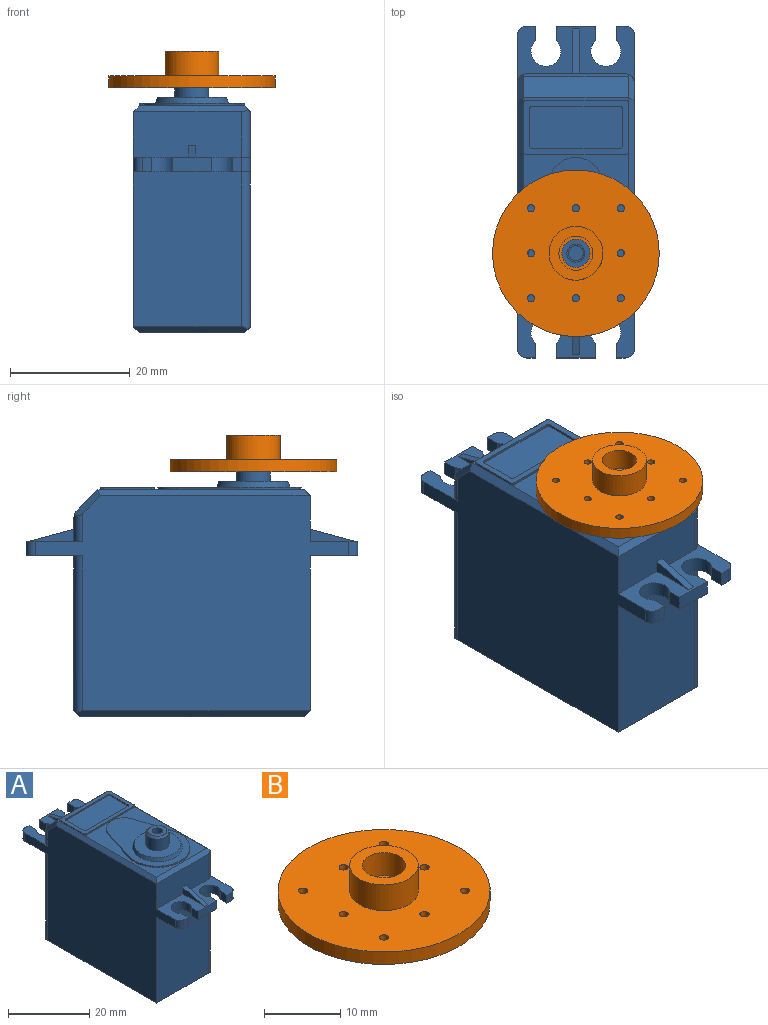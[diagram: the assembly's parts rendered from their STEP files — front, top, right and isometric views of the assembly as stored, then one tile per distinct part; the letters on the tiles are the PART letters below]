
ASSEMBLY  parts=2 mates=1
PART A: 88 faces, bbox 19.5x55.4x43.3 mm
  f0: plane 25.45x17.5mm, normal (0,0,1), area 153.9mm2, adj f42,f43,f44,f45,f56,f57,f58,f77
  f1: plane 17.5x0.91mm, normal (0,0,1), area 7.4mm2, adj f41,f56,f58,f71,f84,f85
  f2: plane 19.5x9.5mm, normal (0,0,1), area 94.3mm2, adj f3,f4,f5,f14,f15,f29,f30,f31
  f3: plane 16.5x3.98mm, normal (0,1,0), area 63.2mm2, adj f2,f36,f37,f38,f60,f61,f62
  f4: plane 2.45x1.5mm, normal (0,1,0), area 3.7mm2, adj f2,f6,f34,f40
  f5: plane 6.5x2.45mm, normal (0,1,0), area 15.9mm2, adj f2,f6,f30,f33
  f6: plane 19.5x9.5mm, normal (0,0,-1), area 103.3mm2, adj f4,f5,f7,f14,f15,f29,f30,f31
  f7: plane 25.85x16.5mm, normal (0,1,0), area 426.5mm2, adj f6,f52,f64,f65
  f8: plane 19.5x9.5mm, normal (0,0,1), area 93.8mm2, adj f9,f10,f11,f14,f15,f17,f18,f19
  f9: plane 18x7.6mm, normal (0,-1,0), area 134.4mm2, adj f8,f14,f24,f25,f26,f57,f63
  f10: plane 6.5x2.45mm, normal (0,-1,0), area 15.9mm2, adj f8,f12,f18,f23
  f11: plane 2.45x1.5mm, normal (0,-1,0), area 3.7mm2, adj f8,f12,f20,f27
  f12: plane 19.5x9.5mm, normal (0,0,-1), area 102.8mm2, adj f10,f11,f13,f14,f15,f17,f18,f19
  f13: plane 25.85x18mm, normal (0,-1,0), area 465.3mm2, adj f12,f14,f53,f66
  f14: plane 52.4x35.9mm, normal (-1,0,0), area 1391.9mm2, adj f2,f6,f8,f9,f12,f13,f27,f39
  f15: plane 52.4x35.9mm, normal (1,0,0), area 1341.7mm2, adj f2,f6,f8,f12,f28,f40,f54,f58
  f16: plane 37.4x17.5mm, normal (0,0,-1), area 654.5mm2, adj f51,f52,f53,f54
  f17: plane 2.45x1.5mm, normal (0,-1,0), area 3.7mm2, adj f8,f12,f21,f28
  f18: plane 2.45x2.41mm, normal (-1,0,0), area 5.9mm2, adj f8,f10,f12,f19
  f19: cylinder r=2.5mm len=5mm, axis (0,0,1), area 29mm2, adj f8,f12,f18,f20
  f20: plane 2.45x2.41mm, normal (1,0,0), area 5.9mm2, adj f8,f11,f12,f19
  f21: plane 2.45x2.41mm, normal (-1,0,0), area 5.9mm2, adj f8,f12,f17,f22
  f22: cylinder r=2.5mm len=5mm, axis (0,0,1), area 29mm2, adj f8,f12,f21,f23
  f23: plane 2.45x2.41mm, normal (1,0,0), area 5.9mm2, adj f8,f10,f12,f22
  f24: plane 7.5x2mm, normal (0,-0.26,0.97), area 9.3mm2, adj f8,f9,f25,f26
  f25: plane 7.5x2mm, normal (1,0,0), area 7.5mm2, adj f8,f9,f24
  f26: plane 7.5x2mm, normal (-1,0,0), area 7.5mm2, adj f8,f9,f24
  f27: cylinder r=1.5mm len=2.45mm, axis (0,0,1), area 5.8mm2, adj f8,f11,f12,f14
  f28: cylinder r=1.5mm len=2.45mm, axis (0,0,-1), area 5.8mm2, adj f8,f12,f15,f17
  f29: plane 2.45x1.5mm, normal (0,1,0), area 3.7mm2, adj f2,f6,f31,f39
  f30: plane 2.45x2.41mm, normal (-1,0,0), area 5.9mm2, adj f2,f5,f6,f32
  f31: plane 2.45x2.41mm, normal (1,0,0), area 5.9mm2, adj f2,f6,f29,f32
  f32: cylinder r=2.5mm len=5mm, axis (0,0,1), area 29mm2, adj f2,f6,f30,f31
  f33: plane 2.45x2.41mm, normal (1,0,0), area 5.9mm2, adj f2,f5,f6,f35
  f34: plane 2.45x2.41mm, normal (-1,0,0), area 5.9mm2, adj f2,f4,f6,f35
  f35: cylinder r=2.5mm len=5mm, axis (0,0,1), area 29mm2, adj f2,f6,f33,f34
  f36: plane 7.5x2mm, normal (0,0.26,0.97), area 9.3mm2, adj f2,f3,f37,f38
  f37: plane 7.5x2mm, normal (1,0,0), area 7.5mm2, adj f2,f3,f36
  f38: plane 7.5x2mm, normal (-1,0,0), area 7.5mm2, adj f2,f3,f36
  f39: cylinder r=1.5mm len=2.45mm, axis (0,0,1), area 5.8mm2, adj f2,f6,f14,f29
  f40: cylinder r=1.5mm len=2.45mm, axis (0,0,-1), area 5.8mm2, adj f2,f4,f6,f15
  f41: plane 17.5x3.56mm, normal (0,0.71,0.71), area 88.1mm2, adj f1,f55,f59,f62
  f42: cylinder r=4.5mm len=8.57mm, axis (0,0,-1), area 4.5mm2, adj f0,f43,f45,f46
  f43: plane 10.43x3.33mm, normal (-0.95,0.3,0), area 4.4mm2, adj f0,f42,f44,f46
  f44: cylinder r=8mm len=16mm, axis (0,0,-1), area 12mm2, adj f0,f43,f45,f46
  f45: plane 10.43x3.33mm, normal (0.95,0.3,0), area 4.4mm2, adj f0,f42,f44,f46
  f46: plane 24x16mm, normal (0,0,1), area 164mm2, adj f42,f43,f44,f45,f48
  f47: plane 11.5x11.5mm, normal (0,0,1), area 78.4mm2, adj f48,f49
  f48: cone r=6.15mm half-angle=21.8deg, axis (0,0,-1), area 40.3mm2, adj f46,f47
  f49: cylinder r=2.85mm len=5.7mm, axis (0,0,-1), area 62.7mm2, adj f47,f67
  f50: plane 4.7x4.7mm, normal (0,0,1), area 12.4mm2, adj f67,f68
  f51: plane 38.96x1mm, normal (-0.71,0,-0.71), area 54mm2, adj f14,f16,f52,f53,f65
  f52: plane 18.62x1mm, normal (0,0.71,-0.71), area 25.5mm2, adj f7,f16,f51,f54,f64,f65
  f53: plane 19.06x1mm, normal (0,-0.71,-0.71), area 25.8mm2, adj f13,f16,f51,f54,f66
  f54: plane 38.52x1mm, normal (0.71,0,-0.71), area 53.6mm2, adj f15,f16,f52,f53,f64,f66
  f55: plane 4.39x4.29mm, normal (-0.71,0.5,0.5), area 7.5mm2, adj f14,f41,f56,f60,f62
  f56: plane 35.4x1mm, normal (-0.71,0,0.71), area 49.1mm2, adj f0,f1,f14,f55,f57,f72
  f57: plane 19.06x1mm, normal (0,-0.71,0.71), area 25.8mm2, adj f0,f9,f56,f58,f63
  f58: plane 34.96x1mm, normal (0.71,0,0.71), area 48.7mm2, adj f0,f1,f15,f57,f59,f63,f70
  f59: plane 4.39x4.29mm, normal (0.71,0.5,0.5), area 7.5mm2, adj f15,f41,f58,f61,f62
  f60: cylinder r=1.5mm len=4.69mm, axis (0,0,1), area 10.2mm2, adj f2,f3,f14,f55,f62
  f61: cylinder r=1.5mm len=4.69mm, axis (0,0,-1), area 10.2mm2, adj f2,f3,f15,f59,f62
  f62: cylinder r=1.5mm len=17.71mm, axis (-1,0,0), area 20.4mm2, adj f3,f41,f55,f59,f60,f61
  f63: cylinder r=1.5mm len=8.04mm, axis (0,0,1), area 18.3mm2, adj f8,f9,f15,f57,f58
  f64: cylinder r=1.5mm len=26.29mm, axis (0,0,-1), area 61.3mm2, adj f6,f7,f15,f52,f54
  f65: cylinder r=1.5mm len=26.29mm, axis (0,0,1), area 61.3mm2, adj f6,f7,f14,f51,f52
  f66: cylinder r=1.5mm len=26.29mm, axis (0,0,1), area 61.3mm2, adj f12,f13,f15,f53,f54
  f67: cone r=2.35mm half-angle=45deg, axis (0,0,-1), area 11.6mm2, adj f49,f50
  f68: cylinder r=1.25mm len=8mm, axis (0,0,1), area 62.8mm2, adj f50,f69
  f69: plane 2.5x2.5mm, normal (0,0,1), area 4.9mm2, adj f68
  f70: plane 8.04x0.4mm, normal (1,0,0), area 3.2mm2, adj f58,f78,f84,f87
  f71: plane 16.5x0.4mm, normal (0,1,0), area 6.6mm2, adj f1,f78,f84,f85
  f72: plane 8.04x0.4mm, normal (-1,0,0), area 3.2mm2, adj f56,f78,f85,f86
  f73: plane 14.5x0.4mm, normal (0,-1,0), area 5.8mm2, adj f78,f79,f80,f83
  f74: plane 6.04x0.4mm, normal (-1,0,0), area 2.4mm2, adj f78,f79,f80,f81
  f75: plane 14.5x0.4mm, normal (0,1,0), area 5.8mm2, adj f78,f79,f81,f82
  f76: plane 6.04x0.4mm, normal (1,0,0), area 2.4mm2, adj f78,f79,f82,f83
  f77: plane 16.5x0.4mm, normal (0,-1,0), area 6.6mm2, adj f0,f78,f86,f87
  f78: plane 17.5x9.04mm, normal (0,0,1), area 49.1mm2, adj f70,f71,f72,f73,f74,f75,f76,f77
  f79: plane 15.5x7.04mm, normal (0,0,1), area 108.8mm2, adj f73,f74,f75,f76,f80,f81,f82,f83
  f80: cylinder r=0.5mm len=0.5mm, axis (0,0,-1), area 0.3mm2, adj f73,f74,f78,f79
  f81: cylinder r=0.5mm len=0.5mm, axis (0,0,1), area 0.3mm2, adj f74,f75,f78,f79
  f82: cylinder r=0.5mm len=0.5mm, axis (0,0,-1), area 0.3mm2, adj f75,f76,f78,f79
  f83: cylinder r=0.5mm len=0.5mm, axis (0,0,1), area 0.3mm2, adj f73,f76,f78,f79
  f84: cylinder r=0.5mm len=0.5mm, axis (0,0,-1), area 0.3mm2, adj f1,f70,f71,f78
  f85: cylinder r=0.5mm len=0.5mm, axis (0,0,-1), area 0.3mm2, adj f1,f71,f72,f78
  f86: cylinder r=0.5mm len=0.5mm, axis (0,0,1), area 0.3mm2, adj f0,f72,f77,f78
  f87: cylinder r=0.5mm len=0.5mm, axis (0,0,1), area 0.3mm2, adj f0,f70,f77,f78
PART B: 18 faces, bbox 27.8x27.8x6.1 mm
  f0: cylinder r=1.5mm len=3mm, axis (0,0,-1), area 8.5mm2, adj f7,f8
  f1: cylinder r=13.9mm len=27.8mm, axis (0,0,-1), area 174.7mm2, adj f2,f3
  f2: plane 27.8x27.8mm, normal (0,0,1), area 534.3mm2, adj f1,f4,f10,f11,f12,f13,f14,f15
  f3: plane 27.8x27.8mm, normal (0,0,-1), area 559.5mm2, adj f1,f9,f10,f11,f12,f13,f14,f15
  f4: cylinder r=4.5mm len=9mm, axis (0,0,-1), area 115.9mm2, adj f2,f5
  f5: plane 9x9mm, normal (0,0,1), area 38.1mm2, adj f4,f6
  f6: cylinder r=2.85mm len=5.7mm, axis (0,0,1), area 66.3mm2, adj f5,f7
  f7: plane 5.7x5.7mm, normal (0,0,1), area 18.4mm2, adj f0,f6
  f8: plane 7x7mm, normal (0,0,-1), area 31.4mm2, adj f0,f9
  f9: cylinder r=3.5mm len=7mm, axis (0,0,-1), area 33mm2, adj f3,f8
  f10: cylinder r=0.6mm len=2mm, axis (0,0,-1), area 7.5mm2, adj f2,f3
  f11: cylinder r=0.6mm len=2mm, axis (0,0,-1), area 7.5mm2, adj f2,f3
  f12: cylinder r=0.6mm len=2mm, axis (0,0,-1), area 7.5mm2, adj f2,f3
  f13: cylinder r=0.6mm len=2mm, axis (0,0,-1), area 7.5mm2, adj f2,f3
  f14: cylinder r=0.6mm len=2mm, axis (0,0,-1), area 7.5mm2, adj f2,f3
  f15: cylinder r=0.6mm len=2mm, axis (0,0,-1), area 7.5mm2, adj f2,f3
  f16: cylinder r=0.6mm len=2mm, axis (0,0,-1), area 7.5mm2, adj f2,f3
  f17: cylinder r=0.6mm len=2mm, axis (0,0,-1), area 7.5mm2, adj f2,f3
PLACE A t=(0.11,-0.11,-21.91)mm
PLACE B t=(0.11,-10.36,18.99)mm
MATE fastened B.f1 <-> A.f48  axis (0,0,1) through (0.11,-10.36,21.39)mm
